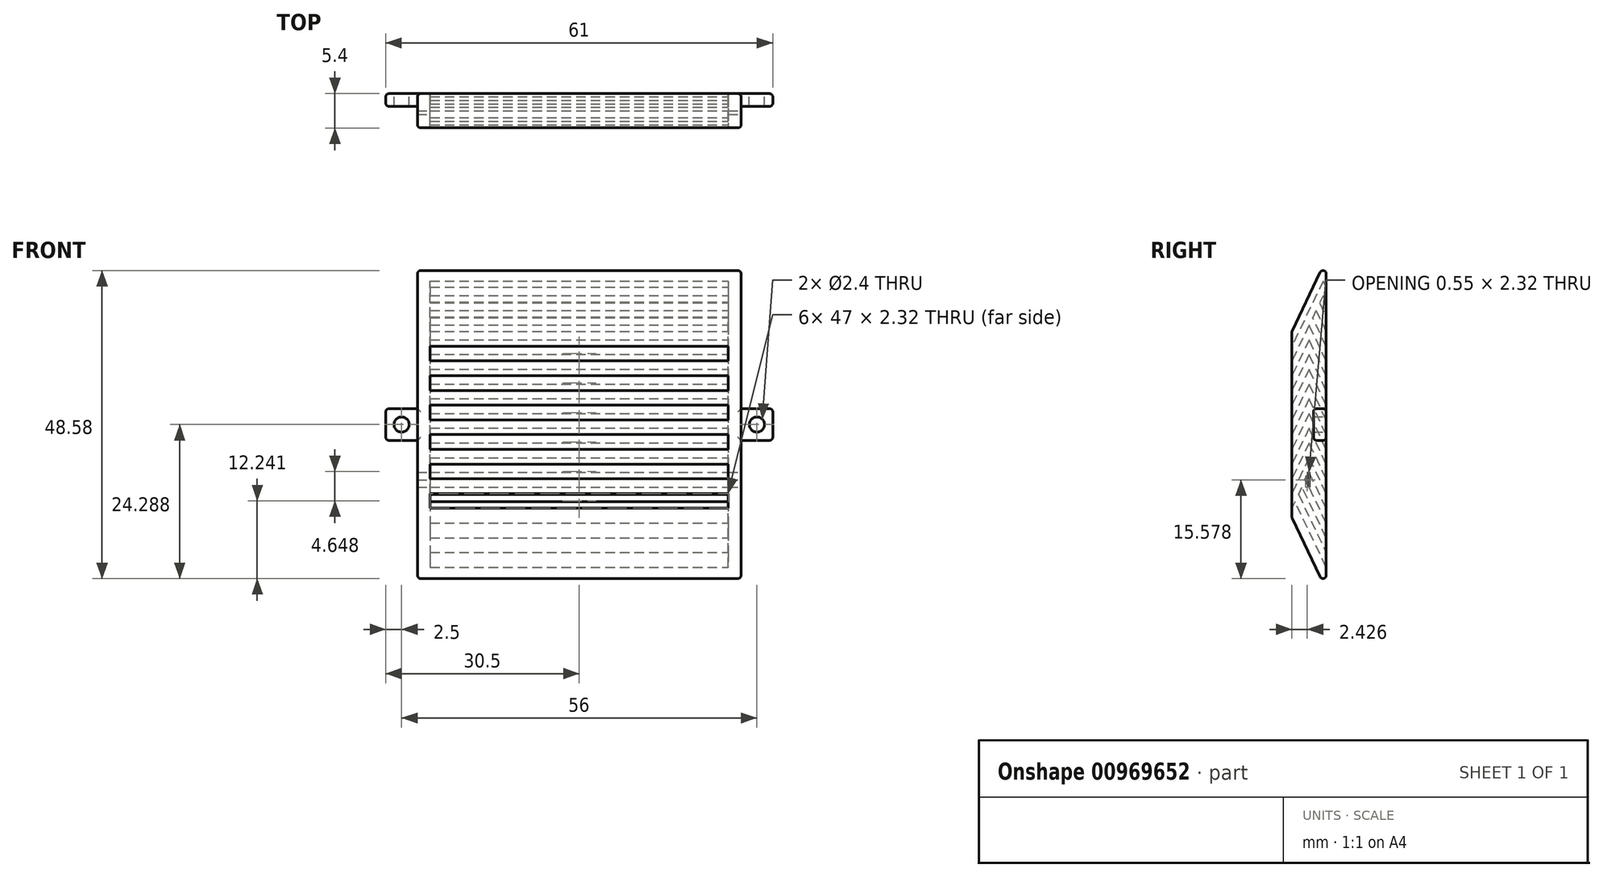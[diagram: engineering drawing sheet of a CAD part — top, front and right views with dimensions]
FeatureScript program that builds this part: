
annotation { "Feature Type Name" : "Feature", "Feature Type Description" : "" }
export const myFeature = defineFeature(function(context is Context, id is Id, definition is map)
    precondition{}
    {
        {
            var Q0;
            Q0=qCreatedBy(makeId("Right.planeOp"),FACE);
            var sketch = newSketch(context, id + "F0", { "sketchPlane" : qUnion([Q0])});
            skLineSegment(sketch, "E0.left", {"start": v(-1.08, 35.02) * mm, "end": v(-1.08, 5.66) * mm});
            skLineSegment(sketch, "E1", {"start": v(-1.08, 35.02) * mm, "end": v(4.32, 46.34) * mm});
            skLineSegment(sketch, "E2", {"start": v(4.32, 46.34) * mm, "end": v(4.32, 34.32) * mm});
            skLineSegment(sketch, "E3", {"start": v(4.32, -5.66) * mm, "end": v(-1.08, 5.66) * mm});
            skPoint(sketch, "E4", {"position": v(1.62, 0) * mm});
            skPoint(sketch, "E5.endSnap0", {"position": v(4.32, 20.34) * mm});
            skLineSegment(sketch, "E6", {"start": v(1.62, 0) * mm, "end": v(1.62, 1.7) * mm});
            skLineSegment(sketch, "E7", {"start": v(-1.08, 11.78) * mm, "end": v(1.62, 17.44) * mm});
            skLineSegment(sketch, "E8", {"start": v(-1.08, 14.1) * mm, "end": v(1.62, 19.76) * mm});
            skLineSegment(sketch, "E9", {"start": v(-1.08, 7.13) * mm, "end": v(-0.6, 8.14) * mm});
            skLineSegment(sketch, "E10", {"start": v(-1.08, 9.45) * mm, "end": v(1.62, 15.11) * mm});
            skLineSegment(sketch, "E11", {"start": v(-1.08, 16.42) * mm, "end": v(1.62, 22.09) * mm});
            skLineSegment(sketch, "E12", {"start": v(-1.08, 18.75) * mm, "end": v(1.62, 24.4) * mm});
            skLineSegment(sketch, "E13", {"start": v(-1.08, 21.07) * mm, "end": v(1.62, 26.73) * mm});
            skLineSegment(sketch, "E14", {"start": v(-1.08, 23.4) * mm, "end": v(1.62, 29.06) * mm});
            skLineSegment(sketch, "E15", {"start": v(-1.08, 25.72) * mm, "end": v(1.62, 31.38) * mm});
            skLineSegment(sketch, "E16", {"start": v(-1.08, 28.04) * mm, "end": v(1.62, 33.7) * mm});
            skPoint(sketch, "E17.startSnap0", {"position": v(0.27, 30.87) * mm});
            skLineSegment(sketch, "E18", {"start": v(-1.08, 30.37) * mm, "end": v(1.62, 36.03) * mm});
            skLineSegment(sketch, "E19", {"start": v(-1.08, 32.7) * mm, "end": v(3.84, 43) * mm});
            skLineSegment(sketch, "E20", {"start": v(4.32, 34.32) * mm, "end": v(4.32, 5.35) * mm});
            skLineSegment(sketch, "E21", {"start": v(4.32, 5.35) * mm, "end": v(4.32, -5.66) * mm});
            skLineSegment(sketch, "E22", {"start": v(1.07, 11.63) * mm, "end": v(4.32, 4.8) * mm});
            skLineSegment(sketch, "E23", {"start": v(1.62, 12.8) * mm, "end": v(4.32, 7.13) * mm});
            skLineSegment(sketch, "E24", {"start": v(1.62, 15.11) * mm, "end": v(4.32, 9.45) * mm});
            skLineSegment(sketch, "E25", {"start": v(1.62, 17.44) * mm, "end": v(4.32, 11.78) * mm});
            skLineSegment(sketch, "E26", {"start": v(1.62, 19.76) * mm, "end": v(4.32, 14.1) * mm});
            skLineSegment(sketch, "E27", {"start": v(1.62, 22.09) * mm, "end": v(4.32, 16.42) * mm});
            skLineSegment(sketch, "E28", {"start": v(1.62, 24.4) * mm, "end": v(4.32, 18.75) * mm});
            skLineSegment(sketch, "E29", {"start": v(1.62, 26.73) * mm, "end": v(4.32, 21.07) * mm});
            skLineSegment(sketch, "E30", {"start": v(1.62, 29.06) * mm, "end": v(4.32, 23.4) * mm});
            skLineSegment(sketch, "E31", {"start": v(1.62, 31.38) * mm, "end": v(4.32, 25.72) * mm});
            skLineSegment(sketch, "E32", {"start": v(1.62, 33.7) * mm, "end": v(4.32, 28.04) * mm});
            skLineSegment(sketch, "E33", {"start": v(1.62, 36.03) * mm, "end": v(4.32, 30.37) * mm});
            skLineSegment(sketch, "E34.trimOffspring", {"start": v(1.62, 38.35) * mm, "end": v(1.62, 40.68) * mm});
            skLineSegment(sketch, "E35.trimOffspring", {"start": v(1.62, 33.7) * mm, "end": v(1.62, 36.03) * mm});
            skLineSegment(sketch, "E36.trimOffspring", {"start": v(1.62, 29.06) * mm, "end": v(1.62, 31.38) * mm});
            skLineSegment(sketch, "E37.trimOffspring", {"start": v(1.62, 24.4) * mm, "end": v(1.62, 26.73) * mm});
            skLineSegment(sketch, "E38.trimOffspring", {"start": v(1.62, 19.76) * mm, "end": v(1.62, 22.09) * mm});
            skLineSegment(sketch, "E39.trimOffspring", {"start": v(1.62, 15.11) * mm, "end": v(1.62, 17.44) * mm});
            skLineSegment(sketch, "E40.trimOffspring", {"start": v(1.62, 10.47) * mm, "end": v(1.62, 12.8) * mm});
            skLineSegment(sketch, "E41.trimOffspring", {"start": v(1.62, 10.47) * mm, "end": v(1.62, 11.02) * mm});
            skLineSegment(sketch, "E42.trimOffspring", {"start": v(1.62, 5.82) * mm, "end": v(1.62, 8.14) * mm});
            skLineSegment(sketch, "E43.trimOffspring", {"start": v(1.62, 1.7) * mm, "end": v(1.62, 3.5) * mm});
            skLineSegment(sketch, "E44", {"start": v(0.52, 10.47) * mm, "end": v(4.32, 2.48) * mm});
            skLineSegment(sketch, "E45", {"start": v(-0.04, 9.3) * mm, "end": v(4.32, 0.16) * mm});
            skLineSegment(sketch, "E46", {"start": v(-0.6, 8.14) * mm, "end": v(4.32, -2.17) * mm});
            skPoint(sketch, "E47.orphan", {"position": v(3.29, 0) * mm});
            skLineSegment(sketch, "E48", {"start": v(2.18, 37.2) * mm, "end": v(2.67, 36.15) * mm});
            skLineSegment(sketch, "E49.trimOffspring", {"start": v(2.18, 37.2) * mm, "end": v(4.32, 32.7) * mm});
            skLineSegment(sketch, "E50.trimOffspring", {"start": v(1.07, 11.63) * mm, "end": v(1.62, 12.8) * mm});
            skLineSegment(sketch, "E51.trimOffspring", {"start": v(-0.04, 9.3) * mm, "end": v(0.52, 10.47) * mm});
            skLineSegment(sketch, "E52.trimOffspring", {"start": v(3.46, 6.6) * mm, "end": v(4.32, 6.56) * mm});
            skLineSegment(sketch, "E53", {"start": v(4.32, 35.02) * mm, "end": v(2.7, 38.4) * mm});
            skLineSegment(sketch, "E54", {"start": v(4.32, 37.34) * mm, "end": v(3.28, 39.51) * mm});
            skLineSegment(sketch, "E55.trimOffspring", {"start": v(2.18, 37.2) * mm, "end": v(2.73, 38.35) * mm});
            skLineSegment(sketch, "E56.trimOffspring", {"start": v(3.28, 39.51) * mm, "end": v(3.84, 40.68) * mm});
            skLineSegment(sketch, "E57", {"start": v(4.32, 39.66) * mm, "end": v(3.84, 40.68) * mm});
            skLineSegment(sketch, "E58", {"start": v(4.32, 41.99) * mm, "end": v(3.84, 43) * mm});
            skLineSegment(sketch, "E59.trimOffspring", {"start": v(2.29, 41.6) * mm, "end": v(2.18, 41.84) * mm});
            skSolve(sketch);
        }
        {
            var Q0;
            Q0 = qSketchRegion(id + "F0", true);
            var Q1;
            {var subQ2=sQuery(id+"F0.wireOp",EDGE,"E41.trimOffspring");Q1=makeQuery(id+"F0.imprint","IMPRINT",FACE,{"disambiguationData":[TD([[makeQuery(id+"F0.imprint","IMPRINT",EDGE,{"derivedFrom":subQ2}),1.0]])]});}
            var Q2;
            {var subQ2=sQuery(id+"F0.wireOp",EDGE,"E42.trimOffspring");Q2=makeQuery(id+"F0.imprint","IMPRINT",FACE,{"disambiguationData":[TD([[makeQuery(id+"F0.imprint","IMPRINT",EDGE,{"derivedFrom":subQ2}),1.0]])]});}
            var Q3;
            {var subQ5=sQuery(id+"F0.wireOp",EDGE,"E42.trimOffspring");Q3=makeQuery(id+"F0.imprint","IMPRINT",FACE,{"disambiguationData":[TD([[makeQuery(id+"F0.imprint","IMPRINT",EDGE,{"derivedFrom":subQ5}),-1.0]])]});}
            var Q4;
            {var subQ5=sQuery(id+"F0.wireOp",EDGE,"5695b0e8-5afb-4637-bdb4-be50a9460034.trimOffspring");Q4=makeQuery(id+"F0.imprint","IMPRINT",FACE,{"disambiguationData":[TD([[makeQuery(id+"F0.imprint","IMPRINT",EDGE,{"derivedFrom":subQ5}),1.0]])]});}
            var Q5;
            {var subQ0=sQuery(id+"F0.wireOp",EDGE,"DSjRrIQA-piG3-6dXx-3wqc-ObfgwwpPwFdc");Q5=makeQuery(id+"F0.imprint","IMPRINT",FACE,{"disambiguationData":[TD([[makeQuery(id+"F0.imprint","IMPRINT",EDGE,{"derivedFrom":subQ0}),-1.0]])]});}
            var Q6;
            {var subQ0=sQuery(id+"F0.wireOp",EDGE,"yDVWCgJg-59xw-ekZ7-0cCH-jzhC7oDVFCRS");var subQ1=sQuery(id+"F0.wireOp",EDGE,"sP1bnbro-JDxn-axZU-fzo1-0zr3MPVD9N3B");var subQ2=makeQuery(id+"F0.imprint","INTERSECT",VERTEX,{"derivedFrom":[subQ1,subQ0]});Q6=makeQuery(id+"F0.imprint","IMPRINT",FACE,{"disambiguationData":[TD([[makeQuery(id+"F0.imprint","IMPRINT",EDGE,{"disambiguationData":[TD([[subQ2,-1.0]])],"derivedFrom":subQ1}),-1.0]])]});}
            extrude(context, id + "F1", {"entities" : qUnion([Q0, Q1, Q2, Q3, Q4, Q5, Q6]), "oppositeDirection" : true, "depth" : 51 * mm, "offsetDistance" : 25.4 * mm});
        }
        {
            var Q0;
            {var subQ6=sQuery(id+"F0.wireOp",EDGE,"E18");Q0=makeQuery(id+"F0.imprint","IMPRINT",FACE,{"disambiguationData":[TD([[makeQuery(id+"F0.imprint","IMPRINT",EDGE,{"derivedFrom":subQ6}),1.0]])]});}
            var Q1;
            {var subQ4=sQuery(id+"F0.wireOp",EDGE,"E15");Q1=makeQuery(id+"F0.imprint","IMPRINT",FACE,{"disambiguationData":[TD([[makeQuery(id+"F0.imprint","IMPRINT",EDGE,{"derivedFrom":subQ4}),1.0]])]});}
            var Q2;
            {var subQ4=sQuery(id+"F0.wireOp",EDGE,"E13");Q2=makeQuery(id+"F0.imprint","IMPRINT",FACE,{"disambiguationData":[TD([[makeQuery(id+"F0.imprint","IMPRINT",EDGE,{"derivedFrom":subQ4}),1.0]])]});}
            var Q3;
            {var subQ4=sQuery(id+"F0.wireOp",EDGE,"E11");Q3=makeQuery(id+"F0.imprint","IMPRINT",FACE,{"disambiguationData":[TD([[makeQuery(id+"F0.imprint","IMPRINT",EDGE,{"derivedFrom":subQ4}),1.0]])]});}
            var Q4;
            {var subQ3=sQuery(id+"F0.wireOp",EDGE,"E7");Q4=makeQuery(id+"F0.imprint","IMPRINT",FACE,{"disambiguationData":[TD([[makeQuery(id+"F0.imprint","IMPRINT",EDGE,{"derivedFrom":subQ3}),1.0]])]});}
            var Q5;
            {var subQ3=sQuery(id+"F0.wireOp",EDGE,"E9");Q5=makeQuery(id+"F0.imprint","IMPRINT",FACE,{"disambiguationData":[TD([[makeQuery(id+"F0.imprint","IMPRINT",EDGE,{"derivedFrom":subQ3}),1.0]])]});}
            var Q6;
            {var subQ9=sQuery(id+"F0.wireOp",EDGE,"DSjRrIQA-piG3-6dXx-3wqc-ObfgwwpPwFdc");Q6=makeQuery(id+"F0.imprint","IMPRINT",FACE,{"disambiguationData":[TD([[makeQuery(id+"F0.imprint","IMPRINT",EDGE,{"derivedFrom":subQ9}),1.0]])]});}
            var Q7;
            {var subQ3=sQuery(id+"F0.wireOp",EDGE,"sP1bnbro-JDxn-axZU-fzo1-0zr3MPVD9N3B");var subQ7=sQuery(id+"F0.wireOp",EDGE,"E43.trimOffspring");var subQ9=makeQuery(id+"F0.imprint","INTERSECT",VERTEX,{"derivedFrom":[subQ3,subQ7]});Q7=makeQuery(id+"F0.imprint","IMPRINT",FACE,{"disambiguationData":[TD([[makeQuery(id+"F0.imprint","IMPRINT",EDGE,{"disambiguationData":[TD([[subQ9,-1.0]])],"derivedFrom":subQ3}),-1.0]])]});}
            var Q8;
            {var subQ0=sQuery(id+"F0.wireOp",EDGE,"E21");var subQ3=sQuery(id+"F0.wireOp",EDGE,"BJKbKunn-9Vcg-HSNy-licZ-ClDGg6NUsFJW");var subQ5=makeQuery(id+"F0.imprint","INTERSECT",VERTEX,{"derivedFrom":[subQ0,subQ3]});Q8=makeQuery(id+"F0.imprint","IMPRINT",FACE,{"disambiguationData":[TD([[makeQuery(id+"F0.imprint","IMPRINT",EDGE,{"disambiguationData":[TD([[subQ5,1.0]])],"derivedFrom":subQ3}),1.0]])]});}
            var Q9;
            {var subQ4=sQuery(id+"F0.wireOp",EDGE,"sP1bnbro-JDxn-axZU-fzo1-0zr3MPVD9N3B");var subQ6=sQuery(id+"F0.wireOp",EDGE,"6gg6mPZa-wPl2-SC5S-lbwv-RbVPXUa9puyq");var subQ8=makeQuery(id+"F0.imprint","INTERSECT",VERTEX,{"derivedFrom":[subQ4,subQ6]});Q9=makeQuery(id+"F0.imprint","IMPRINT",FACE,{"disambiguationData":[TD([[makeQuery(id+"F0.imprint","IMPRINT",EDGE,{"disambiguationData":[TD([[subQ8,-1.0]])],"derivedFrom":subQ4}),-1.0]])]});}
            extrude(context, id + "F2", {"entities" : qUnion([Q0, Q1, Q2, Q3, Q4, Q5, Q6, Q7, Q8, Q9]), "operationType" : NewBodyOperationType.REMOVE, "oppositeDirection" : true, "depth" : 49 * mm, "offsetDistance" : 25.4 * mm});
        }
        {
            var Q0;
            Q0 = qSketchRegion(id + "F0", true);
            extrude(context, id + "F3", {"entities" : qUnion([Q0]), "operationType" : NewBodyOperationType.ADD, "oppositeDirection" : true, "depth" : 2 * mm, "offsetDistance" : 25.4 * mm});
        }
        {
            var Q0;
            Q0=qCreatedBy(makeId("Front.planeOp"),FACE);
            var Q1;
            Q1=sQuery(id+"F0.wireOp",VERTEX,"E1.end");
            cPlane(context, id + "F4", {"entities" : qUnion([Q0, Q1]), "cplaneType" : CPlaneType.PLANE_POINT, "offset" : 25.4 * mm, "width" : 152.4 * mm, "height" : 152.4 * mm});
        }
        {
            var Q0;
            Q0=qCreatedBy(id+"F4.planeOp",FACE);
            var sketch = newSketch(context, id + "F5", { "sketchPlane" : qUnion([Q0])});
            skLineSegment(sketch, "E60.bottom", {"start": v(-51, 22.84) * mm, "end": v(-56, 22.84) * mm});
            skLineSegment(sketch, "E60.top", {"start": v(-51, 17.84) * mm, "end": v(-56, 17.84) * mm});
            skLineSegment(sketch, "E60.left", {"start": v(-51, 22.84) * mm, "end": v(-51, 17.84) * mm});
            skLineSegment(sketch, "E60.right", {"start": v(-56, 22.84) * mm, "end": v(-56, 17.84) * mm});
            skLineSegment(sketch, "E61.bottom", {"start": v(0, 22.84) * mm, "end": v(5, 22.84) * mm});
            skLineSegment(sketch, "E61.top", {"start": v(0, 17.84) * mm, "end": v(5, 17.84) * mm});
            skLineSegment(sketch, "E61.left", {"start": v(0, 22.84) * mm, "end": v(0, 17.84) * mm});
            skLineSegment(sketch, "E61.right", {"start": v(5, 22.84) * mm, "end": v(5, 17.84) * mm});
            skCircle(sketch, "E62", {"center": v(-53.5, 20.34) * mm, "radius": 1.2 * mm});
            skCircle(sketch, "E63", {"center": v(2.5, 20.34) * mm, "radius": 1.2 * mm});
            skLineSegment(sketch, "E64.3", {"start": v(0, 46.34) * mm, "end": v(0, 34.32) * mm});
            skLineSegment(sketch, "E65.0", {"start": v(-51, 46.34) * mm, "end": v(0, 46.34) * mm});
            skLineSegment(sketch, "E66.0", {"start": v(-51, 46.34) * mm, "end": v(-51, -5.66) * mm});
            skLineSegment(sketch, "E67.0", {"start": v(-51, -5.66) * mm, "end": v(0, -5.66) * mm});
            skLineSegment(sketch, "E68.3", {"start": v(0, 34.32) * mm, "end": v(0, 5.35) * mm});
            skLineSegment(sketch, "E68.5", {"start": v(0, 5.35) * mm, "end": v(0, -5.66) * mm});
            skPoint(sketch, "E69", {"position": v(-51, 20.34) * mm});
            skPoint(sketch, "E70", {"position": v(0, 19.84) * mm});
            skSolve(sketch);
        }
        {
            var Q0;
            Q0=makeQuery(id+"F5.imprint","IMPRINT",FACE,{"disambiguationData":[TD([[makeQuery(id+"F5.imprint","IMPRINT",EDGE,{"derivedFrom":sQuery(id+"F5.wireOp",EDGE,"E60.bottom")}),1.0]])]});
            var Q1;
            Q1=makeQuery(id+"F5.imprint","IMPRINT",FACE,{"disambiguationData":[TD([[makeQuery(id+"F5.imprint","IMPRINT",EDGE,{"derivedFrom":sQuery(id+"F5.wireOp",EDGE,"E61.bottom")}),-1.0]])]});
            extrude(context, id + "F6", {"entities" : qUnion([Q0, Q1]), "operationType" : NewBodyOperationType.ADD, "depth" : 2 * mm, "offsetDistance" : 25.4 * mm});
        }
        {
            var Q0;
            Q0=makeQuery(id+"F6.opExtrude","CAP_EDGE",EDGE,{"disambiguationData":[OSD([sQuery(id+"F5.wireOp",EDGE,"E60.bottom")])],"isStart":false});
            var Q1;
            Q1=makeQuery(id+"F6.opExtrude","CAP_EDGE",EDGE,{"disambiguationData":[OSD([sQuery(id+"F5.wireOp",EDGE,"E60.bottom")])],"isStart":true});
            var Q2;
            Q2=makeQuery(id+"F6.opExtrude","SWEPT_EDGE",EDGE,{"disambiguationData":[OSD([sQuery(id+"F5.wireOp",EDGE,"E60.bottom"),sQuery(id+"F5.wireOp",EDGE,"E60.right")])]});
            var Q3;
            Q3=makeQuery(id+"F6.opExtrude","SWEPT_EDGE",EDGE,{"disambiguationData":[OSD([sQuery(id+"F5.wireOp",EDGE,"E60.top"),sQuery(id+"F5.wireOp",EDGE,"E60.right")])]});
            var Q4;
            Q4=makeQuery(id+"F6.opExtrude","CAP_EDGE",EDGE,{"disambiguationData":[OSD([sQuery(id+"F5.wireOp",EDGE,"E60.right")])],"isStart":false});
            var Q5;
            Q5=makeQuery(id+"F6.opExtrude","CAP_EDGE",EDGE,{"disambiguationData":[OSD([sQuery(id+"F5.wireOp",EDGE,"E60.right")])],"isStart":true});
            var Q6;
            Q6=makeQuery(id+"F6.opExtrude","CAP_EDGE",EDGE,{"disambiguationData":[OSD([sQuery(id+"F5.wireOp",EDGE,"E60.top")])],"isStart":false});
            var Q7;
            Q7=makeQuery(id+"F6.opExtrude","CAP_EDGE",EDGE,{"disambiguationData":[OSD([sQuery(id+"F5.wireOp",EDGE,"E60.top")])],"isStart":true});
            var Q8;
            Q8=makeQuery(id+"F6.opExtrude","CAP_EDGE",EDGE,{"disambiguationData":[OSD([sQuery(id+"F5.wireOp",EDGE,"E61.top")])],"isStart":true});
            var Q9;
            Q9=makeQuery(id+"F6.opExtrude","CAP_EDGE",EDGE,{"disambiguationData":[OSD([sQuery(id+"F5.wireOp",EDGE,"E61.bottom")])],"isStart":true});
            var Q10;
            Q10=makeQuery(id+"F6.opExtrude","CAP_EDGE",EDGE,{"disambiguationData":[OSD([sQuery(id+"F5.wireOp",EDGE,"E61.right")])],"isStart":true});
            var Q11;
            Q11=makeQuery(id+"F6.opExtrude","CAP_EDGE",EDGE,{"disambiguationData":[OSD([sQuery(id+"F5.wireOp",EDGE,"E61.top")])],"isStart":false});
            var Q12;
            Q12=makeQuery(id+"F6.opExtrude","SWEPT_EDGE",EDGE,{"disambiguationData":[OSD([sQuery(id+"F5.wireOp",EDGE,"E61.bottom"),sQuery(id+"F5.wireOp",EDGE,"E61.right")])]});
            var Q13;
            Q13=makeQuery(id+"F6.opExtrude","SWEPT_EDGE",EDGE,{"disambiguationData":[OSD([sQuery(id+"F5.wireOp",EDGE,"E61.top"),sQuery(id+"F5.wireOp",EDGE,"E61.right")])]});
            var Q14;
            Q14=makeQuery(id+"F6.opExtrude","CAP_EDGE",EDGE,{"disambiguationData":[OSD([sQuery(id+"F5.wireOp",EDGE,"E61.right")])],"isStart":false});
            var Q15;
            Q15=makeQuery(id+"F6.opExtrude","CAP_EDGE",EDGE,{"disambiguationData":[OSD([sQuery(id+"F5.wireOp",EDGE,"E61.bottom")])],"isStart":false});
            fillet(context, id + "F7", {"entities" : qUnion([Q0, Q1, Q2, Q3, Q4, Q5, Q6, Q7, Q8, Q9, Q10, Q11, Q12, Q13, Q14, Q15]), "radius" : .5 * mm, "tangentPropagation" : true, "allowEdgeOverflow" : false});
        }
        {
            var Q0;
            Q0=makeQuery(id+"F1.opExtrude","SWEPT_EDGE",EDGE,{"disambiguationData":[OSD([sQuery(id+"F0.wireOp",EDGE,"E1"),sQuery(id+"F0.wireOp",EDGE,"E2")])]});
            var Q1;
            Q1=makeQuery(id+"F1.opExtrude","SWEPT_EDGE",EDGE,{"disambiguationData":[OSD([sQuery(id+"F0.wireOp",EDGE,"E3"),sQuery(id+"F0.wireOp",EDGE,"E21")])]});
            var Q2;
            Q2=makeQuery(id+"F1.opExtrude","SWEPT_EDGE",EDGE,{"disambiguationData":[OSD([sQuery(id+"F0.wireOp",EDGE,"E0.left"),sQuery(id+"F0.wireOp",EDGE,"E3"),sQuery(id+"F0.wireOp",EDGE,"sP1bnbro-JDxn-axZU-fzo1-0zr3MPVD9N3B"),sQuery(id+"F0.wireOp",EDGE,"6c48a918-4414-4ec3-81d1-d5293eef4f5a.trimOffspring")])]});
            var Q3;
            Q3=makeQuery(id+"F1.opExtrude","SWEPT_EDGE",EDGE,{"disambiguationData":[OSD([sQuery(id+"F0.wireOp",EDGE,"E0.left"),sQuery(id+"F0.wireOp",EDGE,"E1")])]});
            var Q4;
            Q4=makeQuery(id+"F1.opExtrude","CAP_EDGE",EDGE,{"disambiguationData":[OSD([sQuery(id+"F0.wireOp",EDGE,"E1")])],"isStart":false});
            var Q5;
            Q5=makeQuery(id+"F1.opExtrude","CAP_EDGE",EDGE,{"disambiguationData":[OSD([sQuery(id+"F0.wireOp",EDGE,"E1")])],"isStart":true});
            var Q6;
            {var subQ0=sQuery(id+"F0.wireOp",EDGE,"E0.left");var subQ2=sQuery(id+"F0.wireOp",EDGE,"E3");var subQ3=sQuery(id+"F0.wireOp",EDGE,"E1");var subQ5=makeQuery(id+"F1.opExtrude","CAP_EDGE",EDGE,{"disambiguationData":[OSD([subQ0])],"isStart":true});Q6=makeQuery(id+"F3.boolean.opBoolean","MERGE",EDGE,{"derivedFrom":[makeQuery(id+"F2.boolean.opBoolean","SPLIT",EDGE,{"disambiguationData":[TD([makeQuery(id+"F1.opExtrude","SWEPT_FACE",FACE,{"disambiguationData":[OSD([subQ3])]})])],"derivedFrom":subQ5}),makeQuery(id+"F2.boolean.opBoolean","SPLIT",EDGE,{"disambiguationData":[TD([makeQuery(id+"F1.opExtrude","SWEPT_FACE",FACE,{"disambiguationData":[OSD([subQ2])]})])],"derivedFrom":subQ5}),makeQuery(id+"F2.boolean.opBoolean","SPLIT",EDGE,{"disambiguationData":[TD([makeQuery(id+"F2.opExtrude","SWEPT_FACE",FACE,{"disambiguationData":[OSD([sQuery(id+"F0.wireOp",EDGE,"2TmJhYZk-cNlK-RzkB-OuX1-eWEPF3APuaYp")])]})])],"derivedFrom":subQ5}),makeQuery(id+"F2.boolean.opBoolean","SPLIT",EDGE,{"disambiguationData":[TD([makeQuery(id+"F2.opExtrude","SWEPT_FACE",FACE,{"disambiguationData":[OSD([sQuery(id+"F0.wireOp",EDGE,"E7")])]})])],"derivedFrom":subQ5}),makeQuery(id+"F2.boolean.opBoolean","SPLIT",EDGE,{"disambiguationData":[TD([makeQuery(id+"F2.opExtrude","SWEPT_FACE",FACE,{"disambiguationData":[OSD([sQuery(id+"F0.wireOp",EDGE,"E8")])]})])],"derivedFrom":subQ5}),makeQuery(id+"F2.boolean.opBoolean","SPLIT",EDGE,{"disambiguationData":[TD([makeQuery(id+"F2.opExtrude","SWEPT_FACE",FACE,{"disambiguationData":[OSD([sQuery(id+"F0.wireOp",EDGE,"E12")])]})])],"derivedFrom":subQ5}),makeQuery(id+"F2.boolean.opBoolean","SPLIT",EDGE,{"disambiguationData":[TD([makeQuery(id+"F2.opExtrude","SWEPT_FACE",FACE,{"disambiguationData":[OSD([sQuery(id+"F0.wireOp",EDGE,"E14")])]})])],"derivedFrom":subQ5}),makeQuery(id+"F2.boolean.opBoolean","SPLIT",EDGE,{"disambiguationData":[TD([makeQuery(id+"F2.opExtrude","SWEPT_FACE",FACE,{"disambiguationData":[OSD([sQuery(id+"F0.wireOp",EDGE,"E16")])]})])],"derivedFrom":subQ5}),makeQuery(id+"F3.opExtrude","CAP_EDGE",EDGE,{"disambiguationData":[OSD([subQ0])],"isStart":true})]});}
            var Q7;
            Q7=makeQuery(id+"F1.opExtrude","CAP_EDGE",EDGE,{"disambiguationData":[OSD([sQuery(id+"F0.wireOp",EDGE,"E0.left")])],"isStart":false});
            var Q8;
            Q8=makeQuery(id+"F1.opExtrude","CAP_EDGE",EDGE,{"disambiguationData":[OSD([sQuery(id+"F0.wireOp",EDGE,"E3")])],"isStart":false});
            var Q9;
            Q9=makeQuery(id+"F1.opExtrude","CAP_EDGE",EDGE,{"disambiguationData":[OSD([sQuery(id+"F0.wireOp",EDGE,"E3")])],"isStart":true});
            var Q10;
            {var subQ0=sQuery(id+"F0.wireOp",EDGE,"E21");var subQ1=sQuery(id+"F0.wireOp",EDGE,"E20");var subQ2=sQuery(id+"F0.wireOp",EDGE,"E2");var subQ3=sQuery(id+"F0.wireOp",EDGE,"E1");Q10=makeQuery(id+"F6.boolean.opBoolean","SPLIT",EDGE,{"disambiguationData":[TD([makeQuery(id+"F1.opExtrude","SWEPT_FACE",FACE,{"disambiguationData":[OSD([subQ3])]})])],"derivedFrom":makeQuery(id+"F1.opExtrude","CAP_EDGE",EDGE,{"disambiguationData":[OSD([subQ2,subQ1,subQ0])],"isStart":false})});}
            var Q11;
            {var subQ0=sQuery(id+"F0.wireOp",EDGE,"E3");var subQ1=sQuery(id+"F0.wireOp",EDGE,"E21");var subQ2=sQuery(id+"F0.wireOp",EDGE,"E20");var subQ3=sQuery(id+"F0.wireOp",EDGE,"E2");Q11=makeQuery(id+"F6.boolean.opBoolean","SPLIT",EDGE,{"disambiguationData":[TD([makeQuery(id+"F1.opExtrude","SWEPT_FACE",FACE,{"disambiguationData":[OSD([subQ0])]})])],"derivedFrom":makeQuery(id+"F1.opExtrude","CAP_EDGE",EDGE,{"disambiguationData":[OSD([subQ3,subQ2,subQ1])],"isStart":false})});}
            var Q12;
            {var subQ2=sQuery(id+"F0.wireOp",EDGE,"94APkz6s-wmXF-WRyU-PHZr-5CXPItzwnjKX");var subQ4=sQuery(id+"F0.wireOp",EDGE,"BJKbKunn-9Vcg-HSNy-licZ-ClDGg6NUsFJW");var subQ5=sQuery(id+"F0.wireOp",EDGE,"37smNnaC-x6CY-wBb0-t8l6-9LvpOQsHm04O");var subQ6=sQuery(id+"F0.wireOp",EDGE,"E21");var subQ7=sQuery(id+"F0.wireOp",EDGE,"E20");var subQ10=sQuery(id+"F0.wireOp",EDGE,"E3");var subQ11=sQuery(id+"F0.wireOp",EDGE,"E2");var subQ12=sQuery(id+"F0.wireOp",EDGE,"E1");var subQ16=makeQuery(id+"F1.opExtrude","SWEPT_FACE",FACE,{"disambiguationData":[OSD([subQ12])]});var subQ19=makeQuery(id+"F1.opExtrude","CAP_EDGE",EDGE,{"disambiguationData":[OSD([subQ11,subQ7,subQ6])],"isStart":true});Q12=makeQuery(id+"F6.boolean.opBoolean","SPLIT",EDGE,{"disambiguationData":[TD([subQ16])],"derivedFrom":makeQuery(id+"F3.boolean.opBoolean","MERGE",EDGE,{"derivedFrom":[makeQuery(id+"F2.boolean.opBoolean","SPLIT",EDGE,{"disambiguationData":[TD([subQ16])],"derivedFrom":subQ19}),makeQuery(id+"F2.boolean.opBoolean","SPLIT",EDGE,{"disambiguationData":[TD([makeQuery(id+"F1.opExtrude","SWEPT_FACE",FACE,{"disambiguationData":[OSD([subQ10])]})])],"derivedFrom":subQ19}),makeQuery(id+"F2.boolean.opBoolean","SPLIT",EDGE,{"disambiguationData":[TD([makeQuery(id+"F2.opExtrude","SWEPT_FACE",FACE,{"disambiguationData":[OSD([sQuery(id+"F0.wireOp",EDGE,"f077397f-e586-4444-b6f7-be8b3350ee04.trimOffspring")])]})])],"derivedFrom":subQ19}),makeQuery(id+"F2.boolean.opBoolean","SPLIT",EDGE,{"disambiguationData":[TD([makeQuery(id+"F2.opExtrude","SWEPT_FACE",FACE,{"disambiguationData":[OSD([subQ5])]})])],"derivedFrom":subQ19}),makeQuery(id+"F2.boolean.opBoolean","SPLIT",EDGE,{"disambiguationData":[TD([makeQuery(id+"F2.opExtrude","SWEPT_FACE",FACE,{"disambiguationData":[OSD([sQuery(id+"F0.wireOp",EDGE,"E22")])]})])],"derivedFrom":subQ19}),makeQuery(id+"F2.boolean.opBoolean","SPLIT",EDGE,{"disambiguationData":[TD([makeQuery(id+"F2.opExtrude","SWEPT_FACE",FACE,{"disambiguationData":[OSD([sQuery(id+"F0.wireOp",EDGE,"E24")])]})])],"derivedFrom":subQ19}),makeQuery(id+"F2.boolean.opBoolean","SPLIT",EDGE,{"disambiguationData":[TD([makeQuery(id+"F2.opExtrude","SWEPT_FACE",FACE,{"disambiguationData":[OSD([sQuery(id+"F0.wireOp",EDGE,"E26")])]})])],"derivedFrom":subQ19}),makeQuery(id+"F2.boolean.opBoolean","SPLIT",EDGE,{"disambiguationData":[TD([makeQuery(id+"F2.opExtrude","SWEPT_FACE",FACE,{"disambiguationData":[OSD([sQuery(id+"F0.wireOp",EDGE,"E28")])]})])],"derivedFrom":subQ19}),makeQuery(id+"F2.boolean.opBoolean","SPLIT",EDGE,{"disambiguationData":[TD([makeQuery(id+"F2.opExtrude","SWEPT_FACE",FACE,{"disambiguationData":[OSD([sQuery(id+"F0.wireOp",EDGE,"E30")])]})])],"derivedFrom":subQ19}),makeQuery(id+"F2.boolean.opBoolean","SPLIT",EDGE,{"disambiguationData":[TD([makeQuery(id+"F2.opExtrude","SWEPT_FACE",FACE,{"disambiguationData":[OSD([sQuery(id+"F0.wireOp",EDGE,"E32")])]})])],"derivedFrom":subQ19}),makeQuery(id+"F2.boolean.opBoolean","SPLIT",EDGE,{"disambiguationData":[TD([makeQuery(id+"F2.opExtrude","SWEPT_FACE",FACE,{"disambiguationData":[OSD([sQuery(id+"F0.wireOp",EDGE,"MRET23pb-qrp2-YJN1-3diP-fnRDm7vVgcfm")])]})])],"derivedFrom":subQ19}),makeQuery(id+"F2.boolean.opBoolean","SPLIT",EDGE,{"disambiguationData":[TD([makeQuery(id+"F2.opExtrude","SWEPT_FACE",FACE,{"disambiguationData":[OSD([sQuery(id+"F0.wireOp",EDGE,"GefLgK74-HTF3-5lkp-ur1D-fbonNbbWNGNv")])]})])],"derivedFrom":subQ19}),makeQuery(id+"F2.boolean.opBoolean","SPLIT",EDGE,{"disambiguationData":[TD([makeQuery(id+"F2.opExtrude","SWEPT_FACE",FACE,{"disambiguationData":[OSD([subQ4])]})])],"derivedFrom":subQ19}),makeQuery(id+"F2.boolean.opBoolean","SPLIT",EDGE,{"disambiguationData":[TD([makeQuery(id+"F1.opExtrude","SWEPT_FACE",FACE,{"disambiguationData":[OSD([subQ2])]})])],"derivedFrom":subQ19}),makeQuery(id+"F3.opExtrude","CAP_EDGE",EDGE,{"disambiguationData":[OSD([subQ11,subQ7,subQ6])],"isStart":true})]})});}
            var Q13;
            {var subQ0=sQuery(id+"F0.wireOp",EDGE,"E3");var subQ1=makeQuery(id+"F1.opExtrude","SWEPT_FACE",FACE,{"disambiguationData":[OSD([subQ0])]});var subQ2=sQuery(id+"F0.wireOp",EDGE,"E21");var subQ3=sQuery(id+"F0.wireOp",EDGE,"E20");var subQ4=sQuery(id+"F0.wireOp",EDGE,"E2");var subQ8=sQuery(id+"F0.wireOp",EDGE,"94APkz6s-wmXF-WRyU-PHZr-5CXPItzwnjKX");var subQ10=sQuery(id+"F0.wireOp",EDGE,"BJKbKunn-9Vcg-HSNy-licZ-ClDGg6NUsFJW");var subQ11=sQuery(id+"F0.wireOp",EDGE,"37smNnaC-x6CY-wBb0-t8l6-9LvpOQsHm04O");var subQ14=sQuery(id+"F0.wireOp",EDGE,"E1");var subQ19=makeQuery(id+"F1.opExtrude","CAP_EDGE",EDGE,{"disambiguationData":[OSD([subQ4,subQ3,subQ2])],"isStart":true});Q13=makeQuery(id+"F6.boolean.opBoolean","SPLIT",EDGE,{"disambiguationData":[TD([subQ1])],"derivedFrom":makeQuery(id+"F3.boolean.opBoolean","MERGE",EDGE,{"derivedFrom":[makeQuery(id+"F2.boolean.opBoolean","SPLIT",EDGE,{"disambiguationData":[TD([makeQuery(id+"F1.opExtrude","SWEPT_FACE",FACE,{"disambiguationData":[OSD([subQ14])]})])],"derivedFrom":subQ19}),makeQuery(id+"F2.boolean.opBoolean","SPLIT",EDGE,{"disambiguationData":[TD([subQ1])],"derivedFrom":subQ19}),makeQuery(id+"F2.boolean.opBoolean","SPLIT",EDGE,{"disambiguationData":[TD([makeQuery(id+"F2.opExtrude","SWEPT_FACE",FACE,{"disambiguationData":[OSD([sQuery(id+"F0.wireOp",EDGE,"f077397f-e586-4444-b6f7-be8b3350ee04.trimOffspring")])]})])],"derivedFrom":subQ19}),makeQuery(id+"F2.boolean.opBoolean","SPLIT",EDGE,{"disambiguationData":[TD([makeQuery(id+"F2.opExtrude","SWEPT_FACE",FACE,{"disambiguationData":[OSD([subQ11])]})])],"derivedFrom":subQ19}),makeQuery(id+"F2.boolean.opBoolean","SPLIT",EDGE,{"disambiguationData":[TD([makeQuery(id+"F2.opExtrude","SWEPT_FACE",FACE,{"disambiguationData":[OSD([sQuery(id+"F0.wireOp",EDGE,"E22")])]})])],"derivedFrom":subQ19}),makeQuery(id+"F2.boolean.opBoolean","SPLIT",EDGE,{"disambiguationData":[TD([makeQuery(id+"F2.opExtrude","SWEPT_FACE",FACE,{"disambiguationData":[OSD([sQuery(id+"F0.wireOp",EDGE,"E24")])]})])],"derivedFrom":subQ19}),makeQuery(id+"F2.boolean.opBoolean","SPLIT",EDGE,{"disambiguationData":[TD([makeQuery(id+"F2.opExtrude","SWEPT_FACE",FACE,{"disambiguationData":[OSD([sQuery(id+"F0.wireOp",EDGE,"E26")])]})])],"derivedFrom":subQ19}),makeQuery(id+"F2.boolean.opBoolean","SPLIT",EDGE,{"disambiguationData":[TD([makeQuery(id+"F2.opExtrude","SWEPT_FACE",FACE,{"disambiguationData":[OSD([sQuery(id+"F0.wireOp",EDGE,"E28")])]})])],"derivedFrom":subQ19}),makeQuery(id+"F2.boolean.opBoolean","SPLIT",EDGE,{"disambiguationData":[TD([makeQuery(id+"F2.opExtrude","SWEPT_FACE",FACE,{"disambiguationData":[OSD([sQuery(id+"F0.wireOp",EDGE,"E30")])]})])],"derivedFrom":subQ19}),makeQuery(id+"F2.boolean.opBoolean","SPLIT",EDGE,{"disambiguationData":[TD([makeQuery(id+"F2.opExtrude","SWEPT_FACE",FACE,{"disambiguationData":[OSD([sQuery(id+"F0.wireOp",EDGE,"E32")])]})])],"derivedFrom":subQ19}),makeQuery(id+"F2.boolean.opBoolean","SPLIT",EDGE,{"disambiguationData":[TD([makeQuery(id+"F2.opExtrude","SWEPT_FACE",FACE,{"disambiguationData":[OSD([sQuery(id+"F0.wireOp",EDGE,"MRET23pb-qrp2-YJN1-3diP-fnRDm7vVgcfm")])]})])],"derivedFrom":subQ19}),makeQuery(id+"F2.boolean.opBoolean","SPLIT",EDGE,{"disambiguationData":[TD([makeQuery(id+"F2.opExtrude","SWEPT_FACE",FACE,{"disambiguationData":[OSD([sQuery(id+"F0.wireOp",EDGE,"GefLgK74-HTF3-5lkp-ur1D-fbonNbbWNGNv")])]})])],"derivedFrom":subQ19}),makeQuery(id+"F2.boolean.opBoolean","SPLIT",EDGE,{"disambiguationData":[TD([makeQuery(id+"F2.opExtrude","SWEPT_FACE",FACE,{"disambiguationData":[OSD([subQ10])]})])],"derivedFrom":subQ19}),makeQuery(id+"F2.boolean.opBoolean","SPLIT",EDGE,{"disambiguationData":[TD([makeQuery(id+"F1.opExtrude","SWEPT_FACE",FACE,{"disambiguationData":[OSD([subQ8])]})])],"derivedFrom":subQ19}),makeQuery(id+"F3.opExtrude","CAP_EDGE",EDGE,{"disambiguationData":[OSD([subQ4,subQ3,subQ2])],"isStart":true})]})});}
            fillet(context, id + "F8", {"entities" : qUnion([Q0, Q1, Q2, Q3, Q4, Q5, Q6, Q7, Q8, Q9, Q10, Q11, Q12, Q13]), "radius" : .5 * mm, "tangentPropagation" : true, "allowEdgeOverflow" : false});
        }
    });
